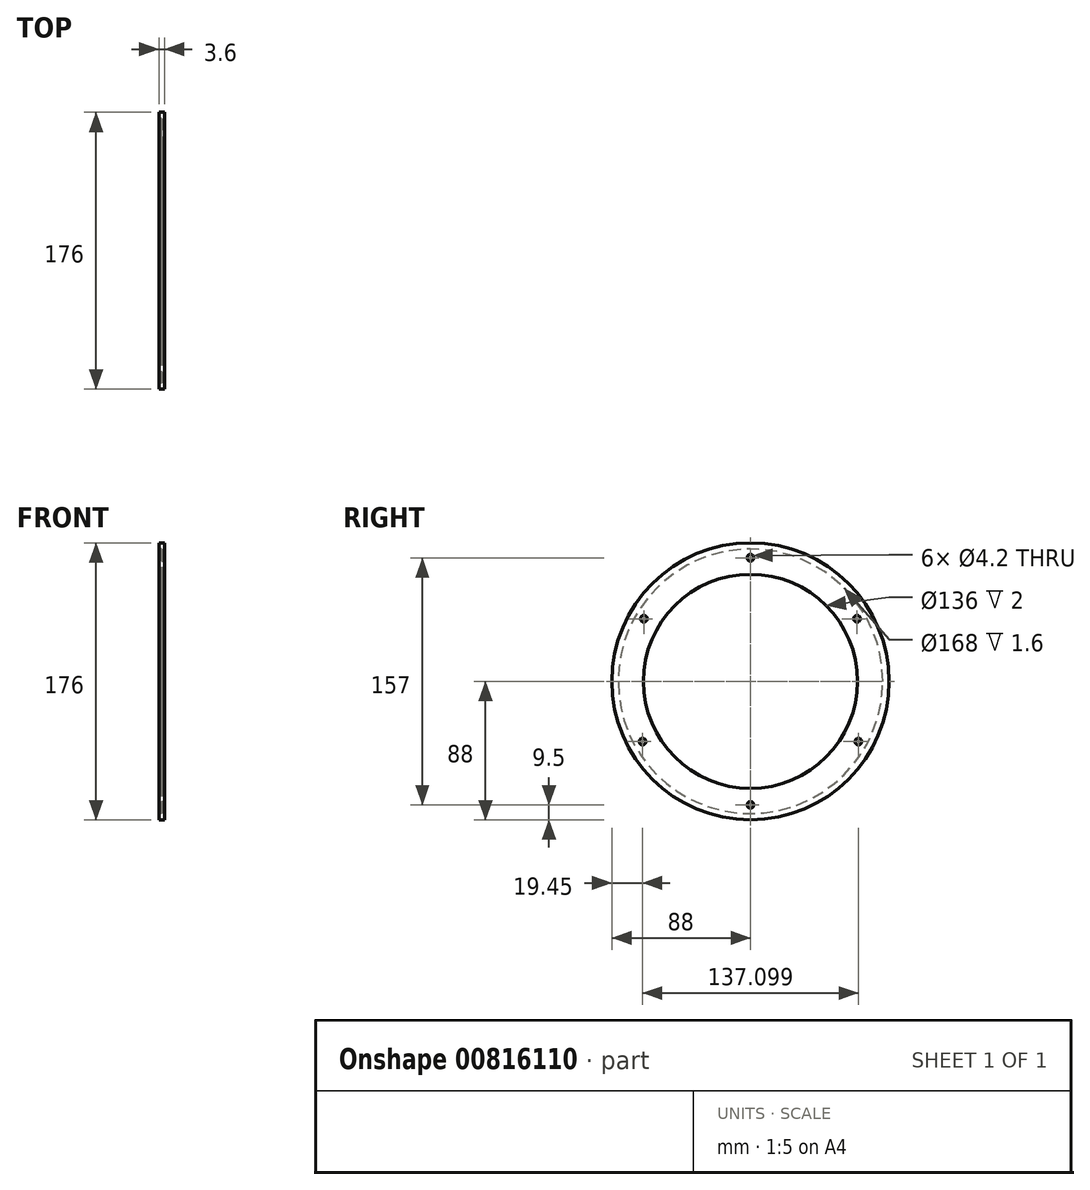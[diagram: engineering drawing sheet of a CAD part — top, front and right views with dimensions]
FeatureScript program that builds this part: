
annotation { "Feature Type Name" : "Feature", "Feature Type Description" : "" }
export const myFeature = defineFeature(function(context is Context, id is Id, definition is map)
    precondition{}
    {
        {
            var Q0;
            Q0=qCreatedBy(makeId("Front.planeOp"),FACE);
            var sketch = newSketch(context, id + "F0", { "sketchPlane" : qUnion([Q0])});
            skLineSegment(sketch, "E0", {"start": v(0, 0) * mm, "end": v(-209.58, 0) * mm, "construction": true});
            skLineSegment(sketch, "E1", {"start": v(-209.58, 0) * mm, "end": v(195.05, 0) * mm, "construction": true});
            skLineSegment(sketch, "E2", {"start": v(195.05, 0) * mm, "end": v(0, 0) * mm, "construction": true});
            skLineSegment(sketch, "E3", {"start": v(-16, 68) * mm, "end": v(16, 68) * mm});
            skLineSegment(sketch, "E4", {"start": v(16, 68) * mm, "end": v(16, 84) * mm});
            skLineSegment(sketch, "E5", {"start": v(16, 84) * mm, "end": v(16.35, 84) * mm});
            skLineSegment(sketch, "E6", {"start": v(16.35, 84) * mm, "end": v(16.35, 88) * mm});
            skLineSegment(sketch, "E7", {"start": v(16.35, 88) * mm, "end": v(-16.35, 88) * mm});
            skLineSegment(sketch, "E8", {"start": v(-16.35, 88) * mm, "end": v(-16.35, 84) * mm});
            skLineSegment(sketch, "E9", {"start": v(-16.35, 84) * mm, "end": v(-16, 84) * mm});
            skLineSegment(sketch, "E10", {"start": v(-16, 84) * mm, "end": v(-16, 68) * mm});
            skLineSegment(sketch, "E11", {"start": v(0, 0) * mm, "end": v(0, 123.2) * mm, "construction": true});
            skSolve(sketch);
        }
        {
            var Q0;
            Q0=qSketchRegion(id+"F0",true);
            var Q1;
            Q1=sQuery(id+"F0.wireOp",EDGE,"E1");
            revolve(context, id + "F1", {"surfaceOperationType" : NewSurfaceOperationType.NEW, "entities" : qUnion([Q0]), "axis" : qUnion([Q1]), "revolveType" : RevolveType.FULL});
        }
        {
            var Q0;
            Q0=makeQuery(id+"F1.opRevolve","SWEPT_FACE",FACE,{"disambiguationData":[OSD([sQuery(id+"F0.wireOp",EDGE,"E6")])]});
            extrude(context, id + "F2", {"entities" : qUnion([Q0]), "operationType" : NewBodyOperationType.REMOVE, "oppositeDirection" : true, "depth" : 0.7 * mm, "offsetDistance" : 25 * mm});
        }
        {
            var Q0;
            Q0=makeQuery(id+"F2.boolean.opBoolean","COPY",FACE,{"derivedFrom":makeQuery(id+"F2.opExtrude","CAP_FACE",FACE,{"disambiguationData":[OSD([sQuery(id+"F0.wireOp",EDGE,"E6")])],"isStart":false})});
            extrude(context, id + "F3", {"entities" : qUnion([Q0]), "operationType" : NewBodyOperationType.ADD, "depth" : 0.35 * mm, "offsetDistance" : 25 * mm});
        }
        {
            var Q0;
            Q0=makeQuery(id+"F3.boolean.opBoolean","MERGE",FACE,{"derivedFrom":[makeQuery(id+"F1.opRevolve","SWEPT_FACE",FACE,{"disambiguationData":[OSD([sQuery(id+"F0.wireOp",EDGE,"E4")])]}),makeQuery(id+"F3.opExtrude","CAP_FACE",FACE,{"disambiguationData":[OSD([sQuery(id+"F0.wireOp",EDGE,"E6")])],"isStart":false})]});
            var sketch = newSketch(context, id + "F4", { "sketchPlane" : qUnion([Q0])});
            skCircle(sketch, "E12", {"center": v(0, 0) * mm, "radius": 78.5 * mm, "construction": true});
            skPoint(sketch, "E13", {"position": v(0, 78.5) * mm});
            skPoint(sketch, "E14", {"position": v(0, -78.5) * mm});
            skPoint(sketch, "E15", {"position": v(68.55, -38.25) * mm});
            skPoint(sketch, "E16", {"position": v(-68.55, -38.25) * mm});
            skPoint(sketch, "E17", {"position": v(-67.7, 39.75) * mm});
            skPoint(sketch, "E18", {"position": v(67.7, 39.75) * mm});
            skSolve(sketch);
        }
        {
            var Q0;
            Q0=sQuery(id+"F4.wireOp",VERTEX,"E17");
            var Q1;
            Q1=sQuery(id+"F4.wireOp",VERTEX,"E13");
            var Q2;
            Q2=sQuery(id+"F4.wireOp",VERTEX,"E18");
            var Q3;
            Q3=sQuery(id+"F4.wireOp",VERTEX,"E15");
            var Q4;
            Q4=sQuery(id+"F4.wireOp",VERTEX,"E14");
            var Q5;
            Q5=sQuery(id+"F4.wireOp",VERTEX,"E16");
            var Q6;
            Q6=makeQuery(id+"F1.opRevolve","SWEPT_BODY",BODY,{"disambiguationData":[OSD([sQuery(id+"F0.wireOp",EDGE,"E3"),sQuery(id+"F0.wireOp",EDGE,"E4"),sQuery(id+"F0.wireOp",EDGE,"E5"),sQuery(id+"F0.wireOp",EDGE,"E6"),sQuery(id+"F0.wireOp",EDGE,"E7"),sQuery(id+"F0.wireOp",EDGE,"E8"),sQuery(id+"F0.wireOp",EDGE,"E9"),sQuery(id+"F0.wireOp",EDGE,"E10")])]});
            hole(context, id + "F5", {"style" : HoleStyle.SIMPLE, "endStyle" : HoleEndStyle.THROUGH, "holeDiameter" : 4.2 * mm, "majorDiameter" : 5 * mm, "isTappedThrough" : true, "tappedDepth" : 12 * mm, "tapClearance" : 3, "locations" : qUnion([Q0, Q1, Q2, Q3, Q4, Q5]), "scope" : qUnion([Q6])});
        }
        {
            var Q0;
            Q0=makeQuery(id+"F1.opRevolve","SWEPT_FACE",FACE,{"disambiguationData":[OSD([sQuery(id+"F0.wireOp",EDGE,"E8")])]});
            extrude(context, id + "F6", {"entities" : qUnion([Q0]), "operationType" : NewBodyOperationType.ADD, "depth" : 1.25 * mm, "offsetDistance" : 25 * mm});
        }
        {
            var Q0;
            Q0=makeQuery(id+"F3.boolean.opBoolean","MERGE",FACE,{"derivedFrom":[makeQuery(id+"F1.opRevolve","SWEPT_FACE",FACE,{"disambiguationData":[OSD([sQuery(id+"F0.wireOp",EDGE,"E4")])]}),makeQuery(id+"F3.opExtrude","CAP_FACE",FACE,{"disambiguationData":[OSD([sQuery(id+"F0.wireOp",EDGE,"E6")])],"isStart":false})]});
            extrude(context, id + "F7", {"entities" : qUnion([Q0]), "operationType" : NewBodyOperationType.REMOVE, "oppositeDirection" : true, "depth" : 30 * mm, "offsetDistance" : 25 * mm});
        }
    });
